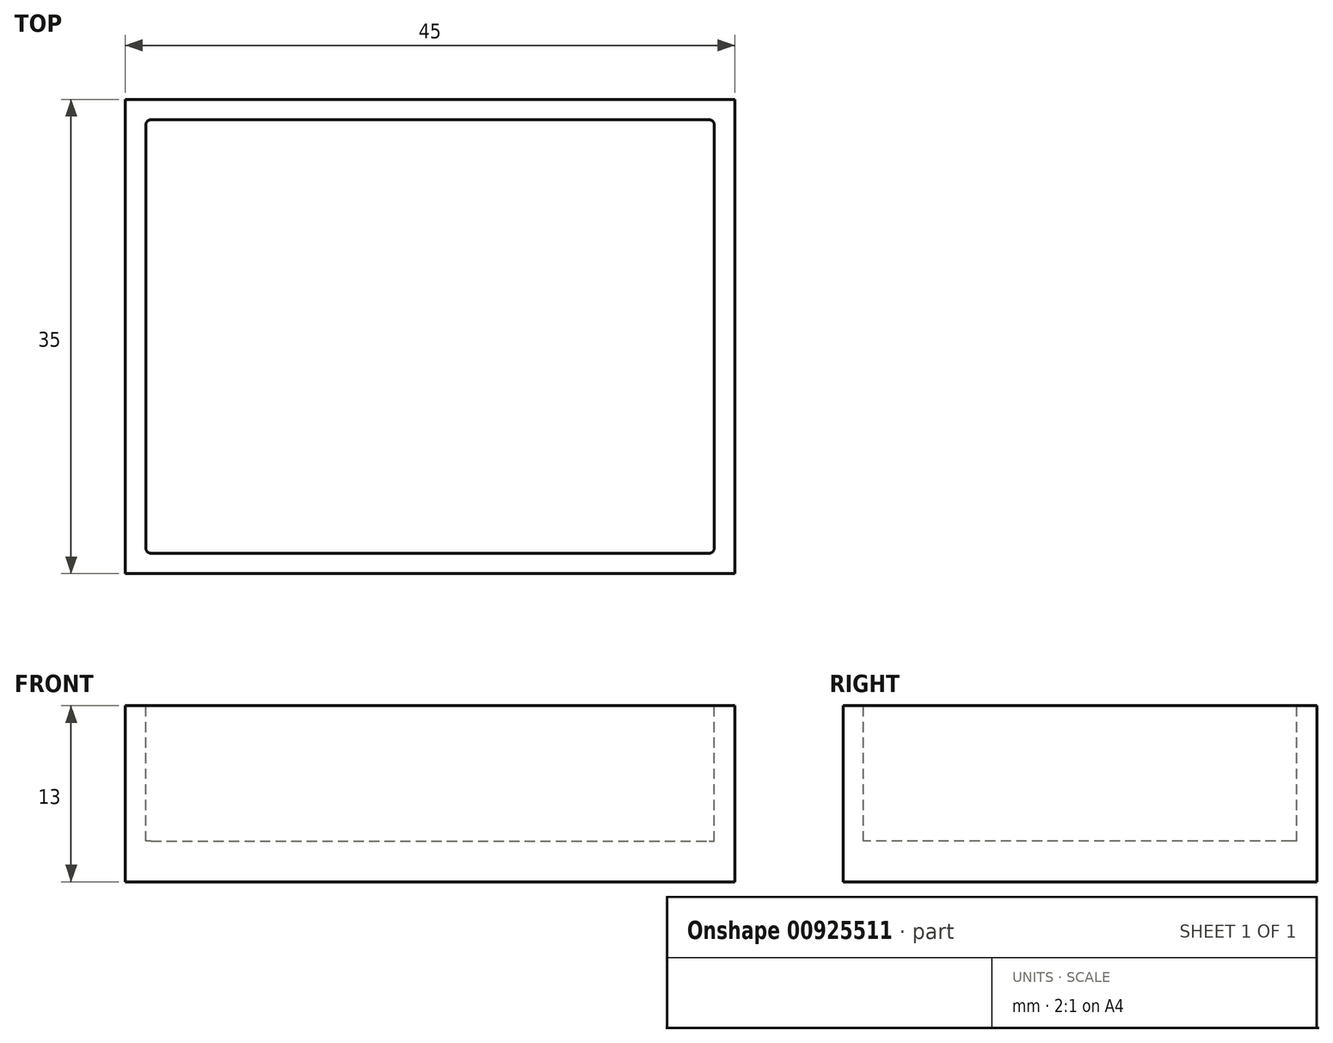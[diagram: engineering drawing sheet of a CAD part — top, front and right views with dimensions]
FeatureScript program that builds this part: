
annotation { "Feature Type Name" : "Feature", "Feature Type Description" : "" }
export const myFeature = defineFeature(function(context is Context, id is Id, definition is map)
    precondition{}
    {
        {
            var Q0;
            Q0=qCreatedBy(makeId("Top.planeOp"),FACE);
            var sketch = newSketch(context, id + "F0", { "sketchPlane" : qUnion([Q0])});
            skLineSegment(sketch, "E0.bottom", {"start": v(-22.5, 17.5) * mm, "end": v(22.5, 17.5) * mm});
            skLineSegment(sketch, "E0.top", {"start": v(-22.5, -17.5) * mm, "end": v(22.5, -17.5) * mm});
            skLineSegment(sketch, "E0.left", {"start": v(-22.5, 17.5) * mm, "end": v(-22.5, -17.5) * mm});
            skLineSegment(sketch, "E0.right", {"start": v(22.5, 17.5) * mm, "end": v(22.5, -17.5) * mm});
            skPoint(sketch, "E0.middle", {"position": v(0, 0) * mm});
            skSolve(sketch);
        }
        {
            var Q0;
            Q0=makeQuery(id+"F0.imprint","IMPRINT",FACE,{"disambiguationData":[TD([[makeQuery(id+"F0.imprint","IMPRINT",EDGE,{"derivedFrom":sQuery(id+"F0.wireOp",EDGE,"E0.bottom")}),-1.0]])]});
            extrude(context, id + "F1", {"entities" : qUnion([Q0]), "depth" : 13 * mm, "offsetDistance" : 25 * mm});
        }
        {
            var Q0;
            Q0=makeQuery(id+"F1.opExtrude","CAP_FACE",FACE,{"disambiguationData":[OSD([sQuery(id+"F0.wireOp",EDGE,"E0.bottom"),sQuery(id+"F0.wireOp",EDGE,"E0.top"),sQuery(id+"F0.wireOp",EDGE,"E0.left"),sQuery(id+"F0.wireOp",EDGE,"E0.right")])],"isStart":false});
            var sketch = newSketch(context, id + "F2", { "sketchPlane" : qUnion([Q0])});
            skLineSegment(sketch, "E1.bottom", {"start": v(-21, 16) * mm, "end": v(21, 16) * mm});
            skLineSegment(sketch, "E1.top", {"start": v(-21, -16) * mm, "end": v(21, -16) * mm});
            skLineSegment(sketch, "E1.left", {"start": v(-21, 16) * mm, "end": v(-21, -16) * mm});
            skLineSegment(sketch, "E1.right", {"start": v(21, 16) * mm, "end": v(21, -16) * mm});
            skPoint(sketch, "E1.middle", {"position": v(0, 0) * mm});
            skSolve(sketch);
        }
        {
            var Q0;
            Q0=makeQuery(id+"F2.imprint","IMPRINT",FACE,{"disambiguationData":[TD([[makeQuery(id+"F2.imprint","IMPRINT",EDGE,{"derivedFrom":sQuery(id+"F2.wireOp",EDGE,"E1.bottom")}),-1.0]])]});
            extrude(context, id + "F3", {"entities" : qUnion([Q0]), "operationType" : NewBodyOperationType.REMOVE, "oppositeDirection" : true, "depth" : 10 * mm, "offsetDistance" : 25 * mm});
        }
        {
            var Q0;
            Q0=makeQuery(id+"F3.boolean.opBoolean","COPY",EDGE,{"derivedFrom":makeQuery(id+"F3.opExtrude","SWEPT_EDGE",EDGE,{"disambiguationData":[OSD([sQuery(id+"F2.wireOp",EDGE,"E1.top"),sQuery(id+"F2.wireOp",EDGE,"E1.left")])]})});
            var Q1;
            Q1=makeQuery(id+"F3.boolean.opBoolean","COPY",EDGE,{"derivedFrom":makeQuery(id+"F3.opExtrude","SWEPT_EDGE",EDGE,{"disambiguationData":[OSD([sQuery(id+"F2.wireOp",EDGE,"E1.top"),sQuery(id+"F2.wireOp",EDGE,"E1.right")])]})});
            var Q2;
            Q2=makeQuery(id+"F3.boolean.opBoolean","COPY",EDGE,{"derivedFrom":makeQuery(id+"F3.opExtrude","SWEPT_EDGE",EDGE,{"disambiguationData":[OSD([sQuery(id+"F2.wireOp",EDGE,"E1.bottom"),sQuery(id+"F2.wireOp",EDGE,"E1.right")])]})});
            var Q3;
            Q3=makeQuery(id+"F3.boolean.opBoolean","COPY",EDGE,{"derivedFrom":makeQuery(id+"F3.opExtrude","SWEPT_EDGE",EDGE,{"disambiguationData":[OSD([sQuery(id+"F2.wireOp",EDGE,"E1.bottom"),sQuery(id+"F2.wireOp",EDGE,"E1.left")])]})});
            fillet(context, id + "F4", {"entities" : qUnion([Q0, Q1, Q2, Q3]), "radius" : 0.4 * mm, "tangentPropagation" : true, "allowEdgeOverflow" : false});
        }
    });
